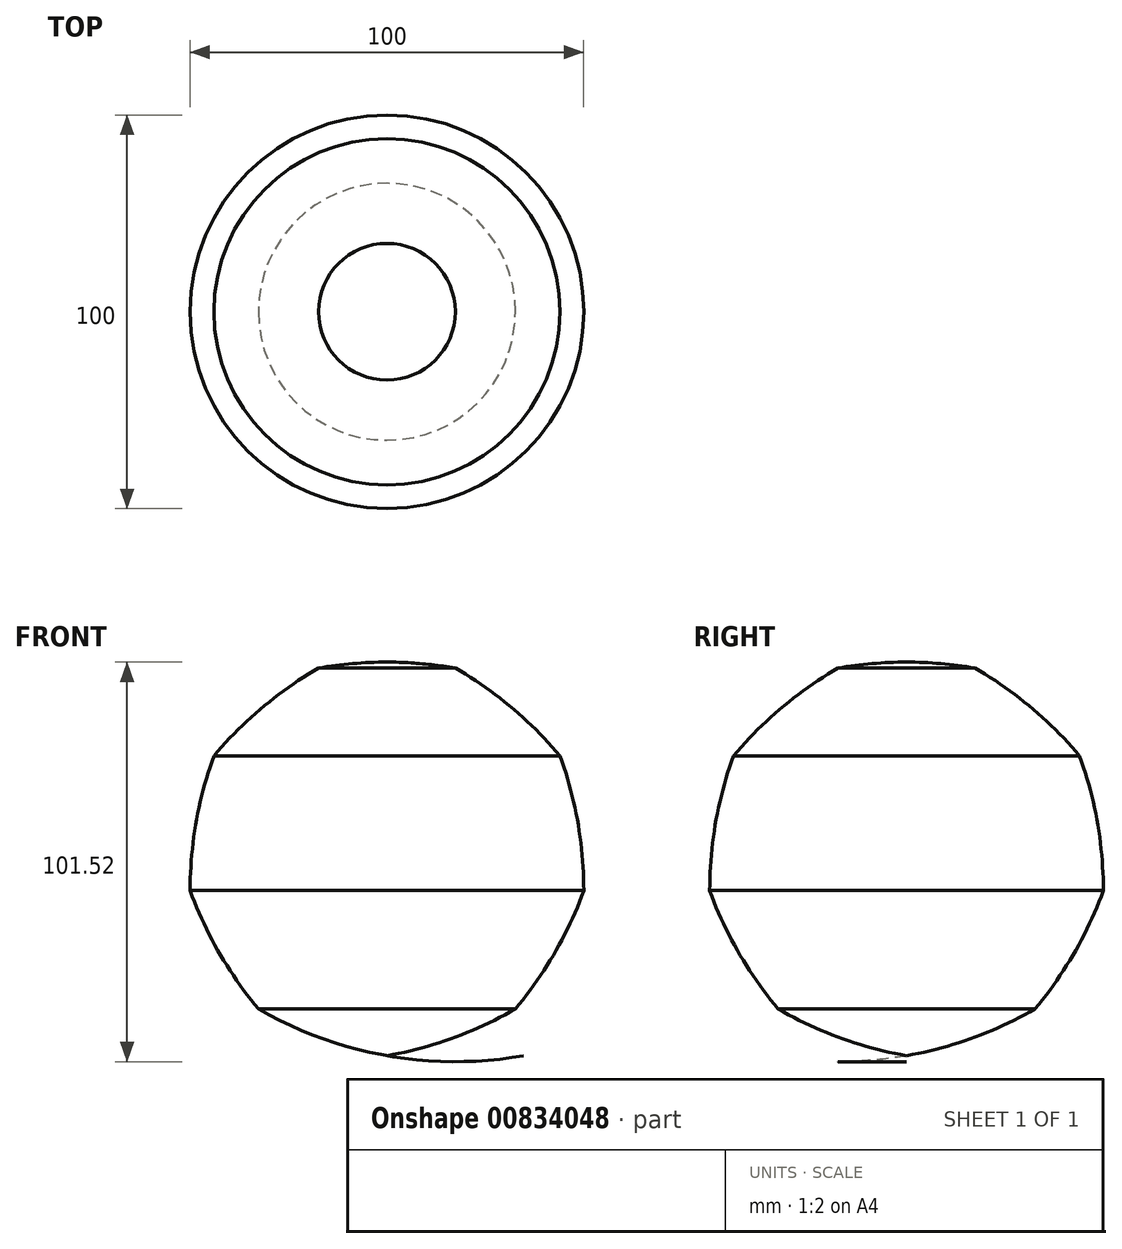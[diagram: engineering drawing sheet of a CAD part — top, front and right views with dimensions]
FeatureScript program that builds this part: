
annotation { "Feature Type Name" : "Feature", "Feature Type Description" : "" }
export const myFeature = defineFeature(function(context is Context, id is Id, definition is map)
    precondition{}
    {
        {
            var Q0;
            Q0=qCreatedBy(makeId("Front.planeOp"),FACE);
            var sketch = newSketch(context, id + "F0", { "sketchPlane" : qUnion([Q0])});
            skArc(sketch, "E0.cCircle", {"start": v(-44.56, 8.28) * mm, "mid": v(33.1, -36.55) * mm, "end": v(2.42, 47.7) * mm, "construction": true});
            skLineSegment(sketch, "E0.0", {"start": v(-14.94, 47.7) * mm, "end": v(19.79, 47.7) * mm, "construction": true});
            skLineSegment(sketch, "E0.1", {"start": v(19.79, 47.7) * mm, "end": v(46.4, 25.39) * mm, "construction": true});
            skLineSegment(sketch, "E0.2", {"start": v(46.4, 25.39) * mm, "end": v(52.42, -8.82) * mm, "construction": true});
            skLineSegment(sketch, "E0.3", {"start": v(52.42, -8.82) * mm, "end": v(35.06, -38.9) * mm, "construction": true});
            skLineSegment(sketch, "E0.4", {"start": v(35.06, -38.9) * mm, "end": v(2.42, -50.77) * mm, "construction": true});
            skLineSegment(sketch, "E0.5", {"start": v(2.42, -50.77) * mm, "end": v(-30.21, -38.9) * mm, "construction": true});
            skLineSegment(sketch, "E0.6", {"start": v(-30.21, -38.9) * mm, "end": v(-47.58, -8.82) * mm, "construction": true});
            skLineSegment(sketch, "E0.7", {"start": v(-47.58, -8.82) * mm, "end": v(-41.54, 25.39) * mm, "construction": true});
            skLineSegment(sketch, "E0.8", {"start": v(-28.24, 36.55) * mm, "end": v(-14.94, 47.7) * mm, "construction": true});
            skPoint(sketch, "E0.0.midPoint", {"position": v(2.42, 47.7) * mm});
            skArc(sketch, "E1", {"start": v(19.79, 47.7) * mm, "mid": v(2.42, 49.23) * mm, "end": v(-14.94, 47.7) * mm});
            skPoint(sketch, "E2", {"position": v(2.42, 49.23) * mm});
            skArc(sketch, "E3", {"start": v(52.42, -8.82) * mm, "mid": v(50.9, 8.55) * mm, "end": v(46.4, 25.39) * mm});
            skArc(sketch, "E4", {"start": v(46.4, 25.39) * mm, "mid": v(34.07, 37.71) * mm, "end": v(19.79, 47.7) * mm});
            skArc(sketch, "E5", {"start": v(35.06, -38.9) * mm, "mid": v(45.06, -24.61) * mm, "end": v(52.42, -8.82) * mm});
            skArc(sketch, "E6", {"start": v(2.42, -50.77) * mm, "mid": v(19.26, -46.26) * mm, "end": v(35.06, -38.9) * mm});
            skArc(sketch, "E7", {"start": v(-47.49, -8.3) * mm, "mid": v(-40.19, -24.36) * mm, "end": v(-30.21, -38.9) * mm});
            skArc(sketch, "E8", {"start": v(-14.94, 47.7) * mm, "mid": v(-29.22, 37.71) * mm, "end": v(-41.54, 25.39) * mm});
            skArc(sketch, "E9", {"start": v(-30.21, -38.9) * mm, "mid": v(-14.41, -46.26) * mm, "end": v(2.42, -50.77) * mm});
            skArc(sketch, "E10", {"start": v(-41.54, 25.39) * mm, "mid": v(-46.06, 8.55) * mm, "end": v(-47.58, -8.82) * mm});
            skLineSegment(sketch, "E11", {"start": v(2.42, 49.23) * mm, "end": v(2.42, -50.77) * mm});
            skSolve(sketch);
        }
        {
            var Q0;
            Q0=makeQuery(id+"F0.imprint","IMPRINT",FACE,{"disambiguationData":[TD([[makeQuery(id+"F0.imprint","IMPRINT",EDGE,{"derivedFrom":sQuery(id+"F0.wireOp",EDGE,"E3")}),1.0]])]});
            var Q1;
            Q1=sQuery(id+"F0.wireOp",EDGE,"E11");
            revolve(context, id + "F1", {"surfaceOperationType" : NewSurfaceOperationType.NEW, "entities" : qUnion([Q0]), "axis" : qUnion([Q1]), "revolveType" : RevolveType.FULL});
        }
    });
